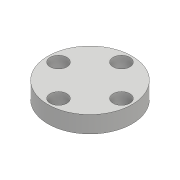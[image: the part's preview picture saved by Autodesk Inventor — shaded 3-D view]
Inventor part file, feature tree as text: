
AUTODESK INVENTOR PART (.ipt)
format: ipt  version: 2017 (Build 210142000, 142)  size: 88,576 bytes
history: native  units: mm
features: extrude x1, sketch x1
ambient origin geometry x8: Origin, YZ Plane, XZ Plane, XY Plane, X Axis, Y Axis, Z Axis, Center Point
bodies: Solid1 (feature_tree)
feature tree (2):
  extrude  "Extrusion1"  Depth=10.0mm
  sketch  "Sketch1"  dims[d0=50.0mm d1=10.0mm d2=40.0mm d4=360.0deg d6=10.0mm d7=0.0mm]
